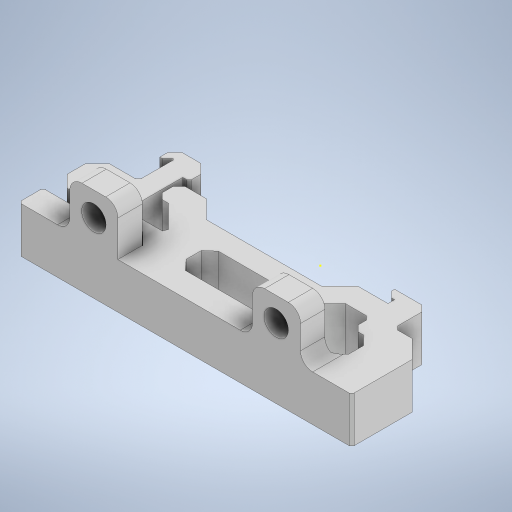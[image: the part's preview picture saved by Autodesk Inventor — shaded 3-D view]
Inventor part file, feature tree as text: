
AUTODESK INVENTOR PART (.ipt)
format: ipt  version: 2024 (Build 280153000, 153)  size: 455,168 bytes
history: native  units: in
note: dims shown in document units (in); Inventor stores cm internally (conversion verified against a paired STEP export)
features: sketch x4, extrude x2, projected_geometry x2, fillet x1, hole x1
ambient origin geometry x8: Origin, YZ Plane, XZ Plane, XY Plane, X Axis, Y Axis, Z Axis, Center Point
bodies: Solid1 (feature_tree)
feature tree (10):
  sketch  "Sketch1"  dims[d0=0.3758in d1=0.1566in d2=0.1762in d3=0.1957in d4=0.1387in d5=0.1174in d6=0.0391in d7=0.0157in d8=2.1217in d9=0.0973in d10=0.0587in d11=0.0587in d12=0.0548in d13=0.0235in d14=0.9395in d15=0.0587in d16=0.0973in d17=0.5854in d18=0.1174in d19=0.7438in d20=0.1174in d21=0.1174in d22=0.137in d23=0.1475in d24=0.0277in d25=0.2143in d26=0.3464in d27=0.0196in d28=0.0626in d29=0.0137in d30=0.0274in d31=0.0607in d32=0.1213in d33=0.047in d34=0.0509in d35=0.0157in d36=0.0356in d37=0.0094in d38=0.2063in d39=0.0196in d40=0.1664in d41=0.0783in d42=0.1174in d43=0.0783in d44=0.4893in d45=0.0783in d46=0.6302in d47=0.0156in d48=0.1253in d49=0.1174in d50=0.1174in d51=0.1174in d52=0.0391in d53=0.0391in d54=0.0391in d55=0.1475in d56=0.0695in d57=0.0391in d58=0.0391in d59=0.0196in d60=0.0196in d61=0.0196in d62=0.0196in d63=0.0196in d64=0.0658in d65=0.0235in d66=0.0587in d67=0.0391in d68=0.0391in d69=0.0391in d70=0.0626in d71=0.0548in d72=0.0156in d73=0.0471in d74=0.0607in d75=0.0137in d76=0.0196in d77=0.094in d78=0.0196in d79=0.0156in d80=0.1376in d81=0.0352in d82=0.2349in d83=0.1566in d84=0.3568in d85=0.1566in d86=0.0115in d87=0.0156in d88=0.0772in d89=0.1751in d90=0.0984in d91=0.118in d92=0.2953in d93=0.0in d94=0.311in]
  extrude  "Extrusion1"  Depth=0.311in
  extrude  "Extrusion2"  Depth=0.311in
  fillet  "Fillet1"  Radius=0.8701in
  hole  "Hole1"  [1 undecoded]
  sketch  "Sketch2"  dims[d95=0.311in d96=0.311in d97=0.8701in]
  sketch  "Sketch3"  dims[d98=2.1217in d99=0.3148in]
  projected_geometry  "Projected Loop1"
  sketch  "Sketch4"  dims[d100=0.1575in d101=0.0in d102=0.0787in d103=0.1575in d104=0.2362in d105=0.1575in d106=0.0787in d107=90.0deg d108=0.3937in d109=0.8108in d112=0.1555in d113=0.1555in d116=1.1791in]
  projected_geometry  "Projected Loop2"
note: 1 required parameter value undecoded (feature->parameter linkage not recoverable at this tier; creation-order binding heuristic only, values carry confidence <= 0.55)
